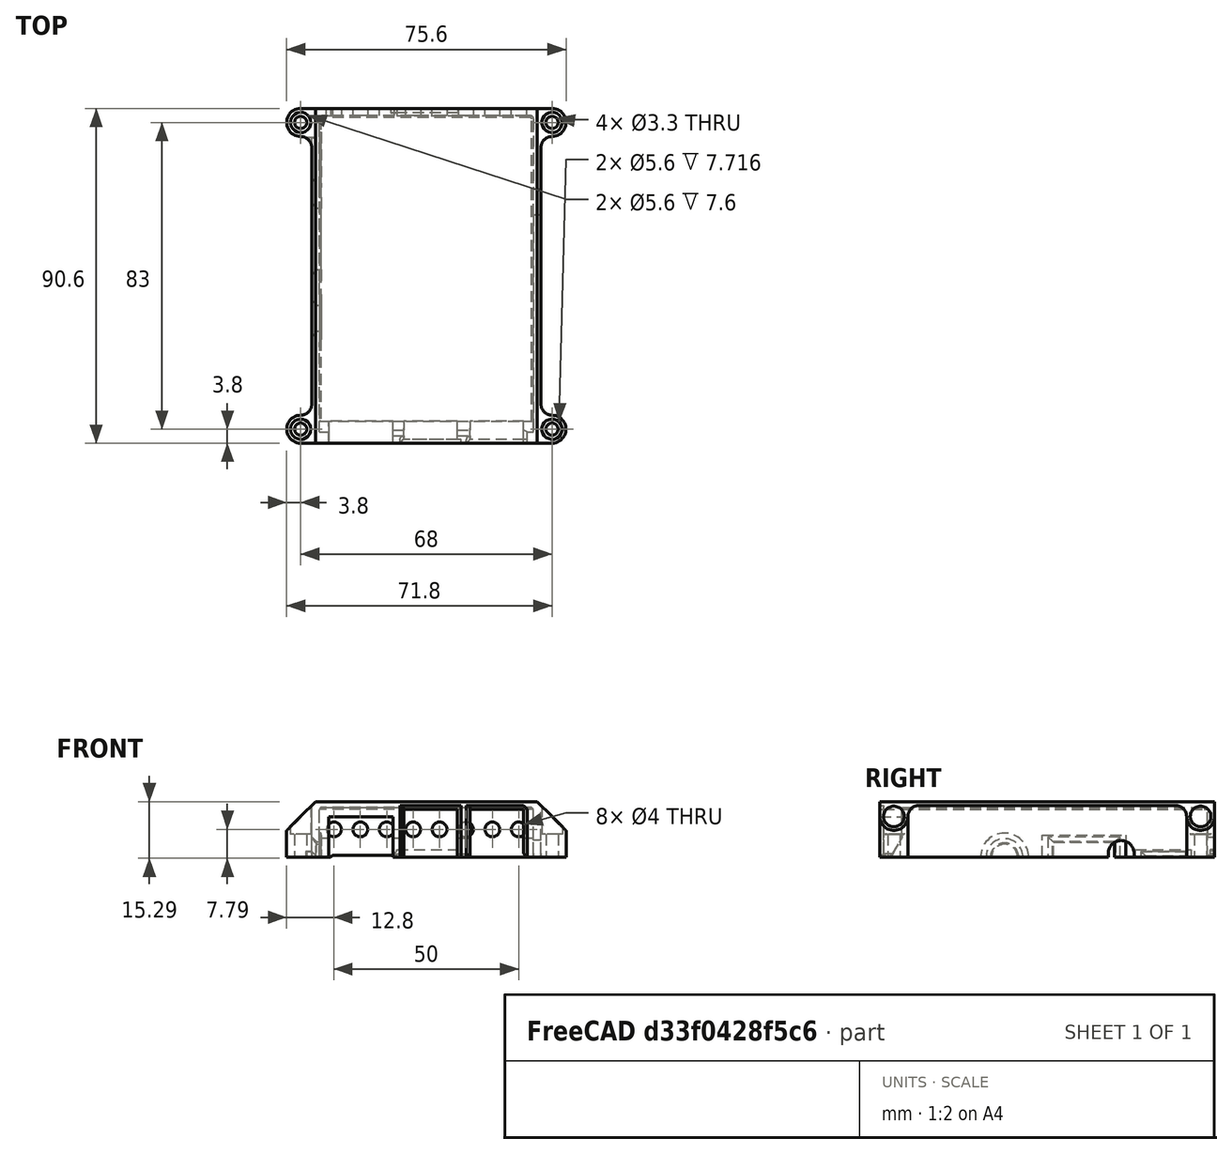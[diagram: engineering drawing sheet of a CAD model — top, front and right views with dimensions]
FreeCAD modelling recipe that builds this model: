
FCSTD DOCUMENT  (FreeCAD 0.22R38495 (Git))
Label: _RPi1RadioKeyborad
License: Creative Commons Attribution 4.0
LicenseURL: https://creativecommons.org/licenses/by/4.0/
objects: Part::Feature×1, Image::ImagePlane×1, Sketcher::SketchObject×1, PartDesign::Body×1
note: 4 computed .brp shape members not serialized (recipe doc carries the construction recipe); baked Part::Feature solids carry a one-line shape summary decoded from their .brp

FEATURE [Part::Feature] Body002  label="Top001"
  Placement = pos=(0,3e-15,-15) rot=(0,0,1;0rad)
  shape: bbox 75.69 x 91.44 x 15.83 mm, 129 faces (baked)
FEATURE [Image::ImagePlane] tastatur
  Placement = pos=(2.5,-1.5,0) rot=(0,0,1;4.71239rad)
  XSize = 117.772
  YSize = 68.5801
FEATURE [Sketcher::SketchObject] Sketch
  ArcFitTolerance = 1e-06
  AttachmentSupport = -> [XY_Plane]
  FullyConstrained = false
  MakeInternals = false
  MapMode = 5
  sketch-geometry (16):
    g0: LineSegment StartX=-20 StartY=-37.5 StartZ=0 EndX=20 EndY=-37.5 EndZ=0
    g1: LineSegment StartX=20 StartY=-37.5 StartZ=0 EndX=20 EndY=37.5 EndZ=0
    g2: LineSegment StartX=20 StartY=37.5 StartZ=0 EndX=-20 EndY=37.5 EndZ=0
    g3: LineSegment StartX=-20 StartY=37.5 StartZ=0 EndX=-20 EndY=-37.5 EndZ=0
    g4: GeomPoint [constr] X=0 Y=0 Z=0
    g5: Circle CenterX=-13.4528 CenterY=-11.3198 CenterZ=0 NormalX=0 NormalY=0 NormalZ=1 AngleXU=0 Radius=2.3
    g6: Circle CenterX=-1.07841 CenterY=-11.3198 CenterZ=0 NormalX=0 NormalY=0 NormalZ=1 AngleXU=0 Radius=2.3
    g7: Circle CenterX=11.296 CenterY=-11.3198 CenterZ=0 NormalX=0 NormalY=0 NormalZ=1 AngleXU=0 Radius=2.3
    g8: Circle CenterX=-1.07841 CenterY=1.05459 CenterZ=0 NormalX=0 NormalY=0 NormalZ=1 AngleXU=0 Radius=2.3
    g9: Circle CenterX=-1.07841 CenterY=-23.6941 CenterZ=0 NormalX=0 NormalY=0 NormalZ=1 AngleXU=0 Radius=2.3
    g10: Circle CenterX=-8.47881 CenterY=21.2367 CenterZ=0 NormalX=0 NormalY=0 NormalZ=1 AngleXU=0 Radius=2.3
    g11: Circle CenterX=11.296 CenterY=21.6802 CenterZ=0 NormalX=0 NormalY=0 NormalZ=1 AngleXU=0 Radius=2.3
    g12: LineSegment [constr] StartX=-1.07841 StartY=1.05459 StartZ=0 EndX=-13.4528 EndY=-11.3198 EndZ=0
    g13: LineSegment [constr] StartX=-1.07841 StartY=1.05459 StartZ=0 EndX=11.296 EndY=-11.3198 EndZ=0
    g14: LineSegment [constr] StartX=11.296 StartY=-11.3198 StartZ=0 EndX=-1.07841 EndY=-23.6941 EndZ=0
    g15: LineSegment [constr] StartX=-1.07841 StartY=-23.6941 StartZ=0 EndX=-13.4528 EndY=-11.3198 EndZ=0
  constraints (37):
    c: Coincident(g0,g1)
    c: Coincident(g1,g2)
    c: Coincident(g2,g3)
    c: Coincident(g3,g0)
    c: Horizontal(g0)
    c: Horizontal(g2)
    c: Vertical(g1)
    c: Vertical(g3)
    c: Symmetric(g2,g0,g4)
    c: Distance(g1,g3) = 40
    c: Distance(g0,g2) = 75
    c: Coincident(g4,g-1)
    c: Diameter(g5) = 4.6
    c: Equal(g5,g6)
    c: Equal(g6,g7)
    c: Equal(g7,g9)
    c: Equal(g9,g8)
    c: Equal(g8,g10)
    c: Equal(g10,g11)
    c: Horizontal(g5,g6)
    c: Horizontal(g6,g7)
    c: Vertical(g9,g6)
    c: Vertical(g6,g8)
    c: Coincident(g12,g8)
    c: Coincident(g12,g5)
    c: Coincident(g13,g8)
    c: Coincident(g13,g7)
    c: Coincident(g14,g7)
    c: Coincident(g14,g9)
    c: Coincident(g15,g9)
    c: Coincident(g15,g5)
    c: Equal(g15,g14)
    c: Equal(g14,g13)
    c: Distance(g15,g15) = 17.5
    c: Perpendicular(g14,g15)
    c: Vertical(g7,g11)
    c: DistanceY(g7,g11) = 33
FEATURE [PartDesign::Body] Body
  AllowCompound = false
  Group = -> [Sketch]
  Origin = -> Origin
